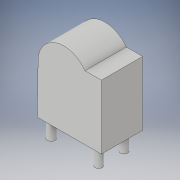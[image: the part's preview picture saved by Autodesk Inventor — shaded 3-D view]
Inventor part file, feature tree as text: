
AUTODESK INVENTOR PART (.ipt)
format: ipt  version: 2019 (Build 230136000, 136)  size: 109,568 bytes
history: native  units: mm
features: extrude x2, sketch x2
ambient origin geometry x8: Origin, YZ Plane, XZ Plane, XY Plane, X Axis, Y Axis, Z Axis, Center Point
bodies: Solid1 (feature_tree)
feature tree (4):
  extrude  "Extrusion1"  Depth=50.0mm TaperAngle=0.0deg
  extrude  "Extrusion2"  [1 undecoded]
  sketch  "Sketch1"  dims[d0=60.0mm d1=50.0mm d2=0.0mm]
  sketch  "Sketch2"  dims[d3=20.0mm d4=0.0mm]
note: 1 required parameter value undecoded (feature->parameter linkage not recoverable at this tier; creation-order binding heuristic only, values carry confidence <= 0.55)
